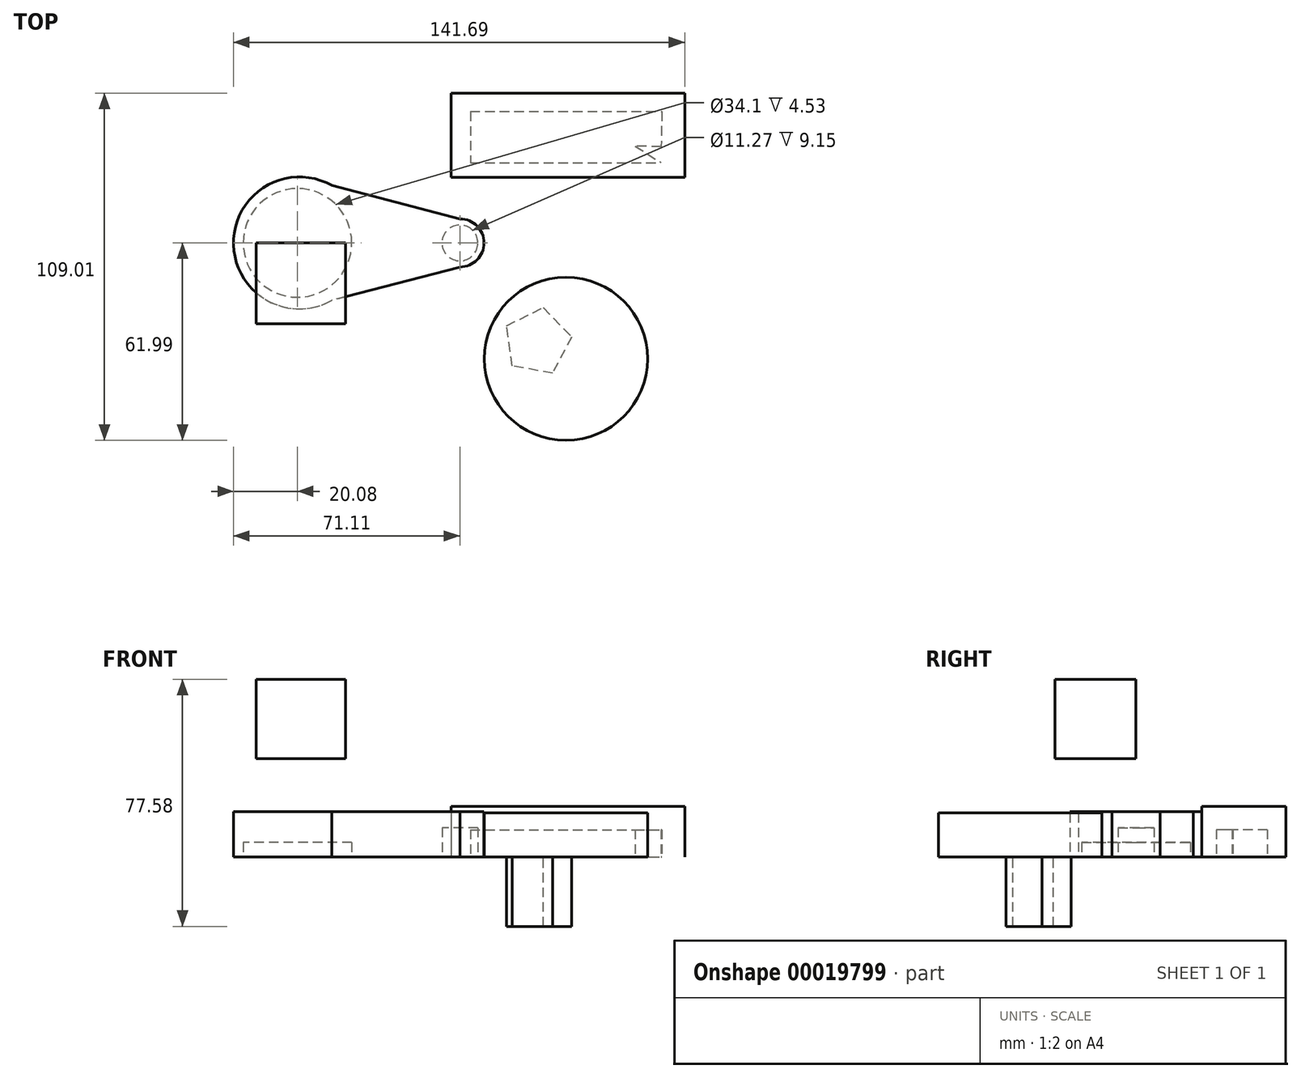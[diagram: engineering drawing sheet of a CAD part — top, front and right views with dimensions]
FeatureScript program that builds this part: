
annotation { "Feature Type Name" : "Feature", "Feature Type Description" : "" }
export const myFeature = defineFeature(function(context is Context, id is Id, definition is map)
    precondition{}
    {
        {
            var Q0;
            Q0=qCreatedBy(makeId("Top.planeOp"),FACE);
            var sketch = newSketch(context, id + "F0", { "sketchPlane" : qUnion([Q0])});
            skCircle(sketch, "E0", {"center": v(-50.4, 0) * mm, "radius": 20.7 * mm});
            skCircle(sketch, "E1", {"center": v(0, 0) * mm, "radius": 7.57 * mm});
            skLineSegment(sketch, "E2", {"start": v(-40.18, 18.01) * mm, "end": v(0, 7.57) * mm});
            skLineSegment(sketch, "E3", {"start": v(0, -7.57) * mm, "end": v(-40.3, -18.08) * mm});
            skSolve(sketch);
        }
        {
            var Q0;
            Q0 = qSketchRegion(id + "F0", true);
            extrude(context, id + "F1", {"entities" : qUnion([Q0]), "depth" : 14.18 * mm});
        }
        {
            var Q0;
            Q0=qCreatedBy(makeId("Top.planeOp"),FACE);
            var sketch = newSketch(context, id + "F2", { "sketchPlane" : qUnion([Q0])});
            skCircle(sketch, "E4", {"center": v(-51.03, 0) * mm, "radius": 17.05 * mm});
            skSolve(sketch);
        }
        {
            var Q0;
            Q0=makeQuery(id+"F2.imprint","IMPRINT",FACE,{"disambiguationData":[TD([[makeQuery(id+"F2.imprint","IMPRINT",EDGE,{"derivedFrom":sQuery(id+"F2.wireOp",EDGE,"E4")}),1.0]])]});
            extrude(context, id + "F3", {"entities" : qUnion([Q0]), "operationType" : NewBodyOperationType.REMOVE, "depth" : 4.53 * mm});
        }
        {
            var Q0;
            Q0=qCreatedBy(makeId("Top.planeOp"),FACE);
            var sketch = newSketch(context, id + "F4", { "sketchPlane" : qUnion([Q0])});
            skCircle(sketch, "E5", {"center": v(0, 0) * mm, "radius": 5.64 * mm});
            skSolve(sketch);
        }
        {
            var Q0;
            Q0=makeQuery(id+"F4.imprint","IMPRINT",FACE,{"disambiguationData":[TD([[makeQuery(id+"F4.imprint","IMPRINT",EDGE,{"derivedFrom":sQuery(id+"F4.wireOp",EDGE,"E5")}),1.0]])]});
            extrude(context, id + "F5", {"entities" : qUnion([Q0]), "operationType" : NewBodyOperationType.REMOVE, "depth" : 9.15 * mm});
        }
        {
            var Q0;
            Q0=qCreatedBy(makeId("Top.planeOp"),FACE);
            var sketch = newSketch(context, id + "F6", { "sketchPlane" : qUnion([Q0])});
            skCircle(sketch, "E6", {"center": v(33.28, -36.38) * mm, "radius": 25.62 * mm});
            skSolve(sketch);
        }
        {
            var Q0;
            Q0=makeQuery(id+"F6.imprint","IMPRINT",FACE,{"disambiguationData":[TD([[makeQuery(id+"F6.imprint","IMPRINT",EDGE,{"derivedFrom":sQuery(id+"F6.wireOp",EDGE,"E6")}),1.0]])]});
            extrude(context, id + "F7", {"entities" : qUnion([Q0]), "depth" : 13.77 * mm});
        }
        {
            var Q0;
            Q0=qCreatedBy(makeId("Top.planeOp"),FACE);
            var sketch = newSketch(context, id + "F8", { "sketchPlane" : qUnion([Q0])});
            skCircle(sketch, "E7.cCircle", {"center": v(24.28, -31.07) * mm, "radius": 8.82 * mm, "construction": true});
            skLineSegment(sketch, "E7.0", {"start": v(35.07, -29.53) * mm, "end": v(29.08, -40.86) * mm});
            skLineSegment(sketch, "E7.1", {"start": v(29.08, -40.86) * mm, "end": v(16.45, -38.65) * mm});
            skLineSegment(sketch, "E7.2", {"start": v(16.45, -38.65) * mm, "end": v(14.65, -25.97) * mm});
            skLineSegment(sketch, "E7.3", {"start": v(14.65, -25.97) * mm, "end": v(26.16, -20.33) * mm});
            skLineSegment(sketch, "E7.4", {"start": v(26.16, -20.33) * mm, "end": v(35.07, -29.53) * mm});
            skPoint(sketch, "E7.0.midPoint", {"position": v(32.08, -35.2) * mm});
            skFitSpline(sketch, "E8", {"points": [v(40.2, -38.12) * mm, v(40.52, -48.2) * mm, v(48.47, -43.7) * mm, v(40.2, -38.12) * mm]});
            skSolve(sketch);
        }
        {
            var Q0;
            Q0=makeQuery(id+"F8.imprint","IMPRINT",FACE,{"disambiguationData":[TD([[makeQuery(id+"F8.imprint","IMPRINT",EDGE,{"derivedFrom":sQuery(id+"F8.wireOp",EDGE,"E7.0")}),-1.0]])]});
            extrude(context, id + "F9", {"entities" : qUnion([Q0]), "operationType" : NewBodyOperationType.ADD, "oppositeDirection" : true, "depth" : 21.82 * mm});
        }
        {
            var Q0;
            Q0=qCreatedBy(makeId("Top.planeOp"),FACE);
            var sketch = newSketch(context, id + "F10", { "sketchPlane" : qUnion([Q0])});
            skLineSegment(sketch, "E9.bottom", {"start": v(-2.74, 47.02) * mm, "end": v(70.58, 47.02) * mm});
            skLineSegment(sketch, "E9.top", {"start": v(-2.74, 20.62) * mm, "end": v(70.58, 20.62) * mm});
            skLineSegment(sketch, "E9.left", {"start": v(-2.74, 47.02) * mm, "end": v(-2.74, 20.62) * mm});
            skLineSegment(sketch, "E9.right", {"start": v(70.58, 47.02) * mm, "end": v(70.58, 20.62) * mm});
            skSolve(sketch);
        }
        {
            var Q0;
            Q0 = qSketchRegion(id + "F8", true);
            var Q1;
            Q1=makeQuery(id+"F7.opExtrude","CAP_FACE",FACE,{"disambiguationData":[OSD([sQuery(id+"F6.wireOp",EDGE,"E6")])],"isStart":true});
            var Q2;
            Q2 = qSketchRegion(id + "F10", true);
            extrude(context, id + "F11", {"entities" : qUnion([Q0, Q1, Q2]), "operationType" : NewBodyOperationType.ADD, "depth" : 0.15 * mm});
        }
        {
            var Q0;
            Q0 = qSketchRegion(id + "F10", true);
            var Q1;
            Q1=makeQuery(id+"F11.opExtrude","CAP_FACE",FACE,{"disambiguationData":[OSD([sQuery(id+"F10.wireOp",EDGE,"E9.bottom"),sQuery(id+"F10.wireOp",EDGE,"E9.top"),sQuery(id+"F10.wireOp",EDGE,"E9.left"),sQuery(id+"F10.wireOp",EDGE,"E9.right")])],"isStart":true});
            extrude(context, id + "F12", {"entities" : qUnion([Q0, Q1]), "operationType" : NewBodyOperationType.ADD, "depth" : 15.8 * mm});
        }
        {
            var Q0;
            Q0=qCreatedBy(makeId("Top.planeOp"),FACE);
            var sketch = newSketch(context, id + "F13", { "sketchPlane" : qUnion([Q0])});
            skLineSegment(sketch, "E10", {"start": v(3.3, 41.24) * mm, "end": v(63.41, 41.24) * mm});
            skLineSegment(sketch, "E11", {"start": v(3.3, 41.24) * mm, "end": v(3.3, 25.21) * mm});
            skLineSegment(sketch, "E12", {"start": v(3.3, 25.21) * mm, "end": v(63.16, 25.21) * mm});
            skLineSegment(sketch, "E13", {"start": v(63.41, 41.24) * mm, "end": v(63.16, 30.22) * mm});
            skLineSegment(sketch, "E14", {"start": v(63.16, 30.22) * mm, "end": v(54.98, 30.41) * mm});
            skLineSegment(sketch, "E15", {"start": v(54.98, 30.41) * mm, "end": v(63.16, 25.21) * mm});
            skSolve(sketch);
        }
        {
            var Q0;
            Q0=makeQuery(id+"F13.imprint","IMPRINT",FACE,{"disambiguationData":[TD([[makeQuery(id+"F13.imprint","IMPRINT",EDGE,{"derivedFrom":sQuery(id+"F13.wireOp",EDGE,"E10")}),-1.0]])]});
            extrude(context, id + "F14", {"entities" : qUnion([Q0]), "operationType" : NewBodyOperationType.REMOVE, "depth" : 8.53 * mm});
        }
        {
            var Q0;
            Q0=qCreatedBy(makeId("Front.planeOp"),FACE);
            var sketch = newSketch(context, id + "F15", { "sketchPlane" : qUnion([Q0])});
            skLineSegment(sketch, "E16.bottom", {"start": v(-63.95, 55.76) * mm, "end": v(-35.9, 55.76) * mm});
            skLineSegment(sketch, "E16.top", {"start": v(-63.95, 30.87) * mm, "end": v(-35.9, 30.87) * mm});
            skLineSegment(sketch, "E16.left", {"start": v(-63.95, 55.76) * mm, "end": v(-63.95, 30.87) * mm});
            skLineSegment(sketch, "E16.right", {"start": v(-35.9, 55.76) * mm, "end": v(-35.9, 30.87) * mm});
            skSolve(sketch);
        }
        {
            var Q0;
            Q0 = qSketchRegion(id + "F15", true);
            extrude(context, id + "F16", {"entities" : qUnion([Q0]), "depth" : 25.4 * mm});
        }
    });
